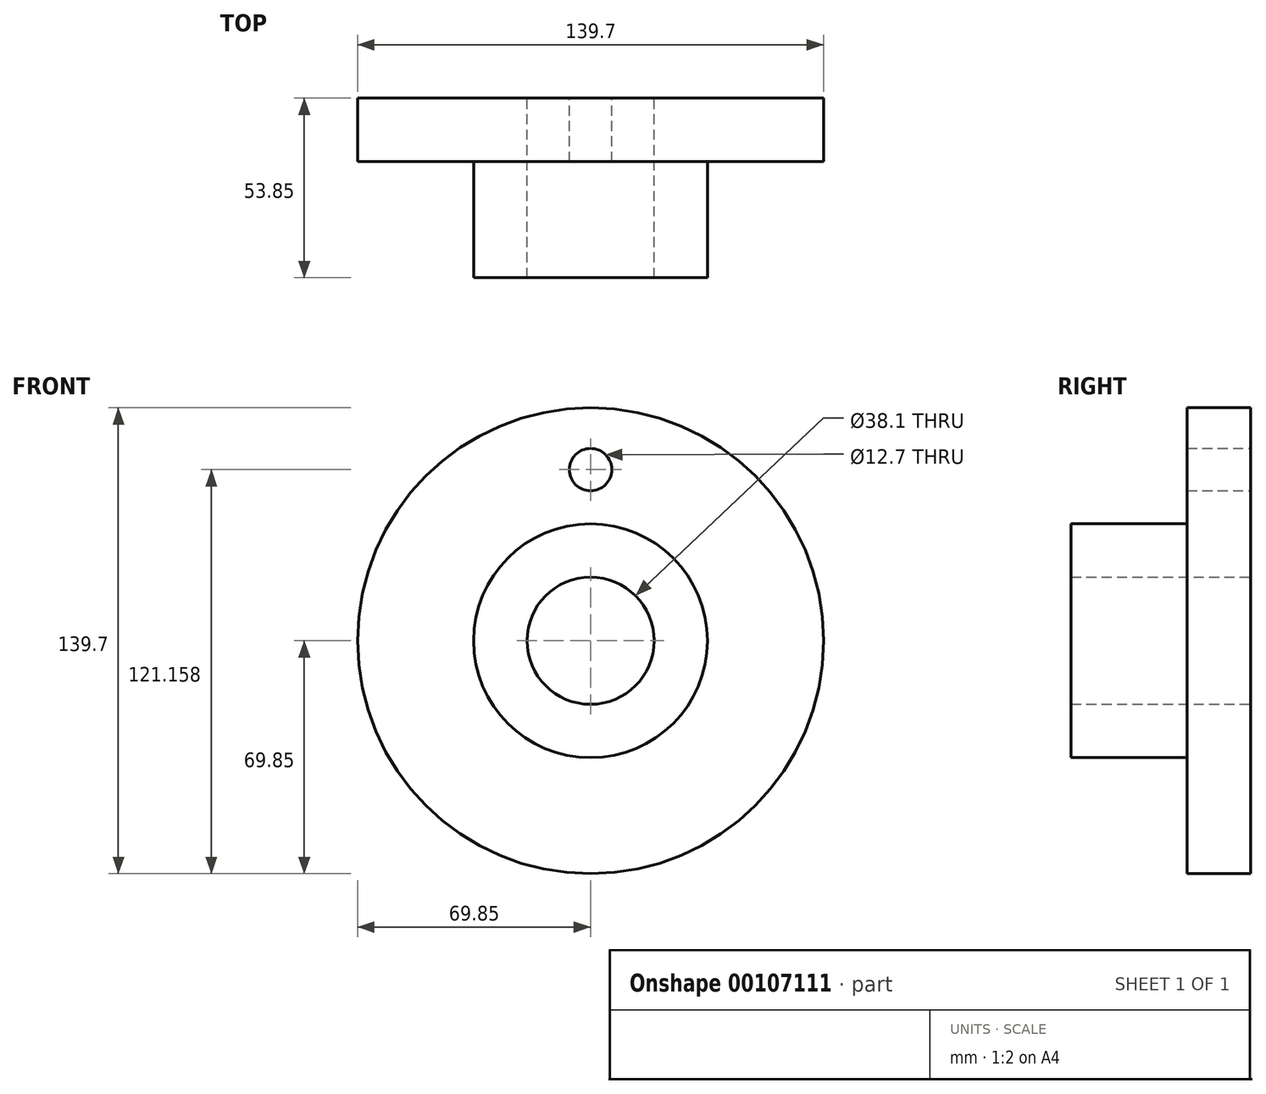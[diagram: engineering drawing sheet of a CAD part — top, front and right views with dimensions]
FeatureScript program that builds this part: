
annotation { "Feature Type Name" : "Feature", "Feature Type Description" : "" }
export const myFeature = defineFeature(function(context is Context, id is Id, definition is map)
    precondition{}
    {
        {
            var Q0;
            Q0=qCreatedBy(makeId("Right.planeOp"),FACE);
            var sketch = newSketch(context, id + "F0", { "sketchPlane" : qUnion([Q0])});
            skLineSegment(sketch, "E0", {"start": v(0, 0) * mm, "end": v(-106.87, 0) * mm, "construction": true});
            skLineSegment(sketch, "E1", {"start": v(0, 69.85) * mm, "end": v(0, 19.05) * mm});
            skLineSegment(sketch, "E2", {"start": v(0, 19.05) * mm, "end": v(-53.85, 19.05) * mm});
            skLineSegment(sketch, "E3", {"start": v(-53.85, 19.05) * mm, "end": v(-53.85, 35.05) * mm});
            skLineSegment(sketch, "E4", {"start": v(-53.85, 35.05) * mm, "end": v(-19.05, 35.05) * mm});
            skLineSegment(sketch, "E5", {"start": v(-19.05, 35.05) * mm, "end": v(-19.05, 69.85) * mm});
            skLineSegment(sketch, "E6", {"start": v(-19.05, 69.85) * mm, "end": v(0, 69.85) * mm});
            skSolve(sketch);
        }
        {
            var Q0;
            Q0=makeQuery(id+"F0.imprint","IMPRINT",FACE,{"disambiguationData":[TD([[makeQuery(id+"F0.imprint","IMPRINT",EDGE,{"derivedFrom":sQuery(id+"F0.wireOp",EDGE,"E1")}),-1.0]])]});
            var Q1;
            Q1=sQuery(id+"F0.wireOp",EDGE,"E0");
            revolve(context, id + "F1", {"entities" : qUnion([Q0]), "axis" : qUnion([Q1]), "revolveType" : RevolveType.FULL});
        }
        {
            var Q0;
            Q0=qCreatedBy(makeId("Front.planeOp"),FACE);
            var sketch = newSketch(context, id + "F2", { "sketchPlane" : qUnion([Q0])});
            skCircle(sketch, "E7", {"center": v(0, 51.3) * mm, "radius": 6.35 * mm});
            skSolve(sketch);
        }
        {
            var Q0;
            Q0 = qSketchRegion(id + "F2", true);
            extrude(context, id + "F3", {"entities" : qUnion([Q0]), "operationType" : NewBodyOperationType.REMOVE, "endBound" : BoundingType.THROUGH_ALL, "depth" : 25.4 * mm});
        }
    });
